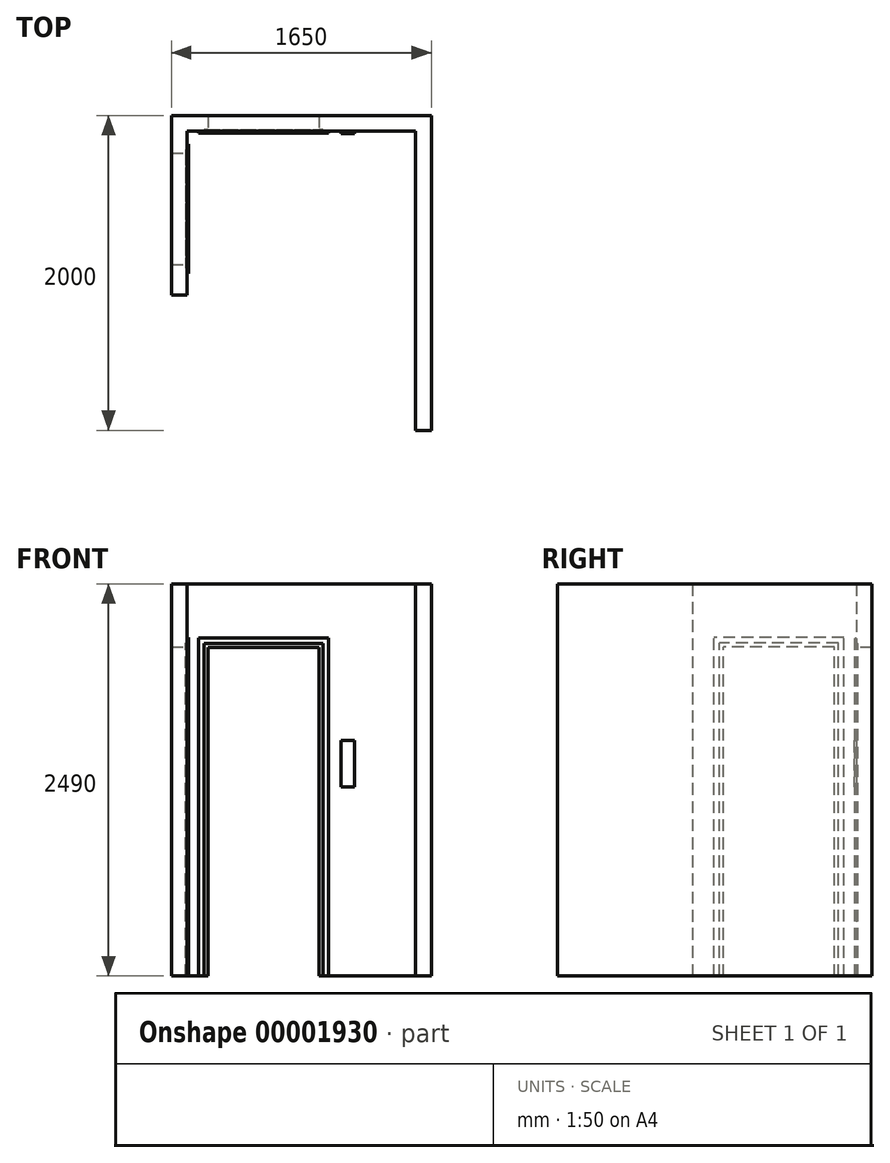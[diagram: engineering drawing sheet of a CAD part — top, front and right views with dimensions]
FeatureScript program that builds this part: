
annotation { "Feature Type Name" : "Feature", "Feature Type Description" : "" }
export const myFeature = defineFeature(function(context is Context, id is Id, definition is map)
    precondition{}
    {
        {
            var Q0;
            Q0=qCreatedBy(makeId("Top.planeOp"),FACE);
            var sketch = newSketch(context, id + "F0", { "sketchPlane" : qUnion([Q0])});
            skLineSegment(sketch, "E0", {"start": v(0, 0) * mm, "end": v(-1450, 0) * mm});
            skLineSegment(sketch, "E1", {"start": v(-1450, 0) * mm, "end": v(-1450, -1040) * mm});
            skLineSegment(sketch, "E2", {"start": v(0, 0) * mm, "end": v(0, -1900) * mm});
            skLineSegment(sketch, "E3.0", {"start": v(-1550, 100) * mm, "end": v(-1550, -1040) * mm});
            skLineSegment(sketch, "E3.1", {"start": v(100, 100) * mm, "end": v(-1550, 100) * mm});
            skLineSegment(sketch, "E3.2", {"start": v(100, 100) * mm, "end": v(100, -1900) * mm});
            skLineSegment(sketch, "E4", {"start": v(-1550, -1040) * mm, "end": v(-1450, -1040) * mm});
            skLineSegment(sketch, "E5", {"start": v(100, -1900) * mm, "end": v(0, -1900) * mm});
            skSolve(sketch);
        }
        {
            var Q0;
            Q0=makeQuery(id+"F0.imprint","IMPRINT",FACE,{"disambiguationData":[TD([[makeQuery(id+"F0.imprint","IMPRINT",EDGE,{"derivedFrom":sQuery(id+"F0.wireOp",EDGE,"E0")}),-1.0]])]});
            extrude(context, id + "F1", {"entities" : qUnion([Q0]), "depth" : (2086 + 25 + 35 + 344) * mm});
        }
        {
            var Q0;
            Q0=makeQuery(id+"F1.opExtrude","SWEPT_FACE",FACE,{"disambiguationData":[OSD([sQuery(id+"F0.wireOp",EDGE,"E1")])]});
            var sketch = newSketch(context, id + "F2", { "sketchPlane" : qUnion([Q0])});
            skLineSegment(sketch, "E6.bottom", {"start": v(-140, 0) * mm, "end": v(-845, 0) * mm});
            skLineSegment(sketch, "E6.top", {"start": v(-140, 2091) * mm, "end": v(-845, 2091) * mm});
            skLineSegment(sketch, "E6.left", {"start": v(-140, 0) * mm, "end": v(-140, 2091) * mm});
            skLineSegment(sketch, "E6.right", {"start": v(-845, 0) * mm, "end": v(-845, 2091) * mm});
            skLineSegment(sketch, "E7.0", {"start": v(-115, 0) * mm, "end": v(-115, 2116) * mm});
            skLineSegment(sketch, "E7.1", {"start": v(-115, 2116) * mm, "end": v(-870, 2116) * mm});
            skLineSegment(sketch, "E7.2", {"start": v(-870, -0.7) * mm, "end": v(-870, 2116) * mm});
            skLineSegment(sketch, "E8.0", {"start": v(5, -5) * mm, "end": v(-1045, -5) * mm});
            skLineSegment(sketch, "E8.1", {"start": v(5, 2495) * mm, "end": v(5, -5) * mm});
            skLineSegment(sketch, "E8.2", {"start": v(5, 2495) * mm, "end": v(-1045, 2495) * mm});
            skLineSegment(sketch, "E8.3", {"start": v(-1045, 2495) * mm, "end": v(-1045, -5) * mm});
            skLineSegment(sketch, "E9.0", {"start": v(-80, 0) * mm, "end": v(-80, 2151) * mm});
            skLineSegment(sketch, "E9.1", {"start": v(-80, 2151) * mm, "end": v(-905, 2151) * mm});
            skLineSegment(sketch, "E9.2", {"start": v(-905, -0.7) * mm, "end": v(-905, 2151) * mm});
            skSolve(sketch);
        }
        {
            var Q0;
            Q0=makeQuery(id+"F2.imprint","IMPRINT",FACE,{"disambiguationData":[TD([[makeQuery(id+"F2.imprint","IMPRINT",EDGE,{"derivedFrom":sQuery(id+"F2.wireOp",EDGE,"E6.bottom")}),-1.0]])]});
            extrude(context, id + "F3", {"entities" : qUnion([Q0]), "operationType" : NewBodyOperationType.REMOVE, "endBound" : BoundingType.THROUGH_ALL, "oppositeDirection" : true, "depth" : 25 * mm});
        }
        {
            var Q0;
            Q0=makeQuery(id+"F2.imprint","IMPRINT",FACE,{"disambiguationData":[TD([[makeQuery(id+"F2.imprint","IMPRINT",EDGE,{"derivedFrom":sQuery(id+"F2.wireOp",EDGE,"E6.top")}),-1.0]])]});
            extrude(context, id + "F4", {"entities" : qUnion([Q0]), "operationType" : NewBodyOperationType.REMOVE, "oppositeDirection" : true, "depth" : 10 * mm});
        }
        {
            var Q0;
            {var subQ6=sQuery(id+"F2.wireOp",EDGE,"E7.0");Q0=makeQuery(id+"F2.imprint","IMPRINT",FACE,{"disambiguationData":[TD([[makeQuery(id+"F2.imprint","IMPRINT",EDGE,{"derivedFrom":subQ6}),-1.0]])]});}
            extrude(context, id + "F5", {"entities" : qUnion([Q0]), "operationType" : NewBodyOperationType.ADD, "depth" : 10 * mm});
        }
        {
            var Q0;
            Q0=makeQuery(id+"F1.opExtrude","SWEPT_FACE",FACE,{"disambiguationData":[OSD([sQuery(id+"F0.wireOp",EDGE,"E0")])]});
            var sketch = newSketch(context, id + "F6", { "sketchPlane" : qUnion([Q0])});
            skLineSegment(sketch, "E10.bottom", {"start": v(-1317, 0) * mm, "end": v(-612, 0) * mm});
            skLineSegment(sketch, "E10.top", {"start": v(-1317, 2086) * mm, "end": v(-612, 2086) * mm});
            skLineSegment(sketch, "E10.left", {"start": v(-1317, 0) * mm, "end": v(-1317, 2086) * mm});
            skLineSegment(sketch, "E10.right", {"start": v(-612, 0) * mm, "end": v(-612, 2086) * mm});
            skLineSegment(sketch, "E11.0", {"start": v(-587, 0) * mm, "end": v(-587, 2111) * mm});
            skLineSegment(sketch, "E11.1", {"start": v(-1342, 2111) * mm, "end": v(-587, 2111) * mm});
            skLineSegment(sketch, "E11.2", {"start": v(-1342, 0) * mm, "end": v(-1342, 2111) * mm});
            skLineSegment(sketch, "E12.0", {"start": v(-552, 0) * mm, "end": v(-552, 2146) * mm});
            skLineSegment(sketch, "E12.1", {"start": v(-1377, 2146) * mm, "end": v(-552, 2146) * mm});
            skLineSegment(sketch, "E12.2", {"start": v(-1377, 0) * mm, "end": v(-1377, 2146) * mm});
            skSolve(sketch);
        }
        {
            var Q0;
            Q0=makeQuery(id+"F6.imprint","IMPRINT",FACE,{"disambiguationData":[TD([[makeQuery(id+"F6.imprint","IMPRINT",EDGE,{"derivedFrom":sQuery(id+"F6.wireOp",EDGE,"E10.bottom")}),-1.0]])]});
            extrude(context, id + "F7", {"entities" : qUnion([Q0]), "operationType" : NewBodyOperationType.REMOVE, "endBound" : BoundingType.THROUGH_ALL, "oppositeDirection" : true, "depth" : 25 * mm});
        }
        {
            var Q0;
            {var subQ2=sQuery(id+"F6.wireOp",EDGE,"E11.0");Q0=makeQuery(id+"F6.imprint","IMPRINT",FACE,{"disambiguationData":[TD([[makeQuery(id+"F6.imprint","IMPRINT",EDGE,{"derivedFrom":subQ2}),-1.0]])]});}
            extrude(context, id + "F8", {"entities" : qUnion([Q0]), "operationType" : NewBodyOperationType.ADD, "depth" : 10 * mm});
        }
        {
            var Q0;
            Q0=makeQuery(id+"F6.imprint","IMPRINT",FACE,{"disambiguationData":[TD([[makeQuery(id+"F6.imprint","IMPRINT",EDGE,{"derivedFrom":sQuery(id+"F6.wireOp",EDGE,"E10.top")}),1.0]])]});
            extrude(context, id + "F9", {"entities" : qUnion([Q0]), "operationType" : NewBodyOperationType.REMOVE, "oppositeDirection" : true, "depth" : 10 * mm});
        }
        {
            var Q0;
            {var subQ4=sQuery(id+"F6.wireOp",EDGE,"E12.0");Q0=makeQuery(id+"F6.imprint","IMPRINT",FACE,{"disambiguationData":[TD([[makeQuery(id+"F6.imprint","IMPRINT",EDGE,{"derivedFrom":subQ4}),-1.0]])]});}
            var sketch = newSketch(context, id + "F10", { "sketchPlane" : qUnion([Q0])});
            skLineSegment(sketch, "E13.bottom", {"start": v(-472, 1495) * mm, "end": v(-387, 1495) * mm});
            skLineSegment(sketch, "E13.top", {"start": v(-472, 1200) * mm, "end": v(-387, 1200) * mm});
            skLineSegment(sketch, "E13.left", {"start": v(-472, 1495) * mm, "end": v(-472, 1200) * mm});
            skLineSegment(sketch, "E13.right", {"start": v(-387, 1495) * mm, "end": v(-387, 1200) * mm});
            skSolve(sketch);
        }
        {
            var Q0;
            Q0=makeQuery(id+"F10.imprint","IMPRINT",FACE,{"disambiguationData":[TD([[makeQuery(id+"F10.imprint","IMPRINT",EDGE,{"derivedFrom":sQuery(id+"F10.wireOp",EDGE,"E13.bottom")}),-1.0]])]});
            extrude(context, id + "F11", {"entities" : qUnion([Q0]), "operationType" : NewBodyOperationType.ADD, "depth" : 15 * mm});
        }
    });
